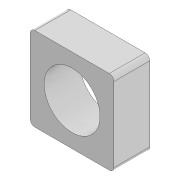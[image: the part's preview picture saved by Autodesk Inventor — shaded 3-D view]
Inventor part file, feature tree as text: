
AUTODESK INVENTOR PART (.ipt)
format: ipt  version: 2022 (Build 260153000, 153)  size: 118,784 bytes
history: native  units: mm
features: extrude x2, sketch x2, fillet x1, projected_geometry x1
ambient origin geometry x8: Origin, YZ Plane, XZ Plane, XY Plane, X Axis, Y Axis, Z Axis, Center Point
bodies: Volumenkörper1 (feature_tree)
feature tree (6):
  extrude  "Extrusion1"  Depth=18.0mm
  fillet  "Rundung1"  Radius=12.0mm
  extrude  "Extrusion2"  Depth=1.0mm
  sketch  "Skizze1"  dims[d0=18.0mm d1=18.0mm d2=12.0mm]
  sketch  "Skizze2"  dims[d3=7.7mm d4=0.0mm d5=1.0mm d6=1.5mm d7=1.5mm d8=10.5mm d9=10.5mm d10=4.2mm d11=4.2mm d12=4.3mm d13=0.0mm]
  projected_geometry  "Projizierte Kontur1"
